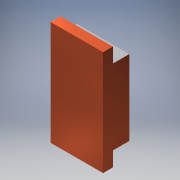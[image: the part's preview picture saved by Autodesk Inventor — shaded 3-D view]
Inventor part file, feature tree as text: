
AUTODESK INVENTOR PART (.ipt)
format: ipt  version: 2016 (Build 200138000, 138)  size: 105,472 bytes
history: native  units: mm
features: extrude x2, sketch x2
ambient origin geometry x8: Origin, YZ Plane, XZ Plane, XY Plane, X Axis, Y Axis, Z Axis, Center Point
bodies: Solid1 (feature_tree)
feature tree (4):
  extrude  "Extrusion1"  Depth=1.15mm
  extrude  "Extrusion2"  Depth=0.25mm TaperAngle=0.0deg
  sketch  "Sketch1"  dims[d2=0.15mm d3=0.0mm d4=1.15mm]
  sketch  "Sketch2"  dims[d5=0.225mm d6=0.25mm d7=0.0mm]
